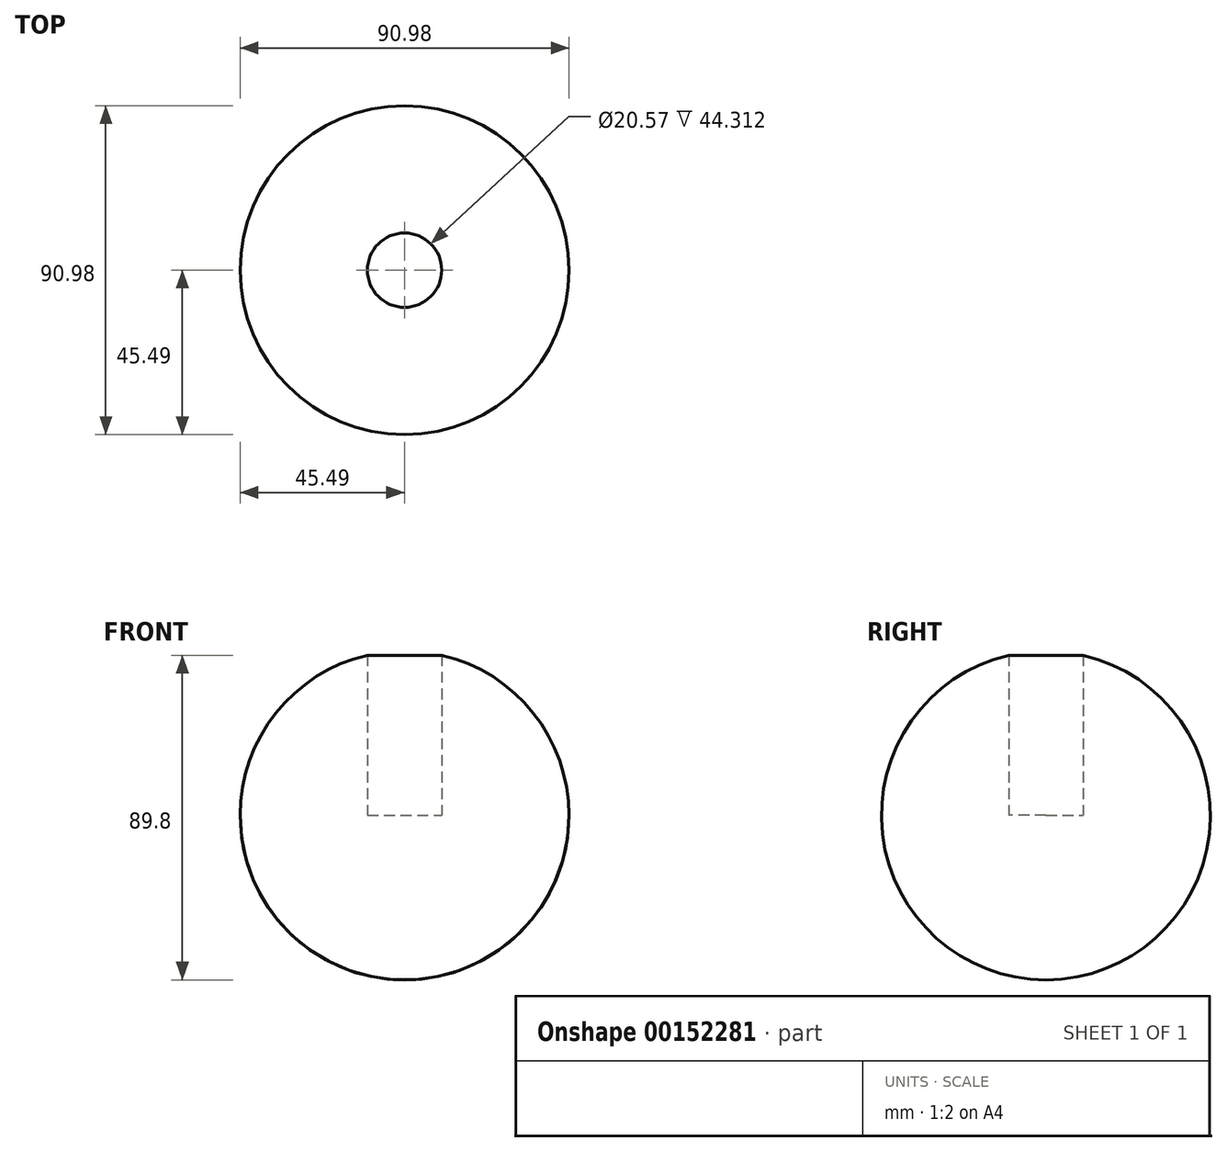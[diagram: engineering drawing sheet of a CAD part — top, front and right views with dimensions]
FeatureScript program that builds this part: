
annotation { "Feature Type Name" : "Feature", "Feature Type Description" : "" }
export const myFeature = defineFeature(function(context is Context, id is Id, definition is map)
    precondition{}
    {
        {
            var Q0;
            Q0=qCreatedBy(makeId("Front.planeOp"),FACE);
            var sketch = newSketch(context, id + "F0", { "sketchPlane" : qUnion([Q0])});
            skArc(sketch, "E0", {"start": v(-45.5, 0) * mm, "mid": v(0, -45.5) * mm, "end": v(45.5, 0) * mm});
            skLineSegment(sketch, "E1.bottom", {"start": v(57.29, -51.39) * mm, "end": v(-57.29, -51.39) * mm});
            skLineSegment(sketch, "E1.left", {"start": v(57.29, -51.39) * mm, "end": v(57.29, 0) * mm});
            skLineSegment(sketch, "E1.right", {"start": v(-57.29, -51.39) * mm, "end": v(-57.29, 0) * mm});
            skPoint(sketch, "E1.top.start.orphan", {"position": v(57.29, 51.39) * mm});
            skPoint(sketch, "E2.orphan", {"position": v(-57.29, 51.39) * mm});
            skLineSegment(sketch, "E3.trimOffspring", {"start": v(45.5, 0) * mm, "end": v(57.29, 0) * mm});
            skLineSegment(sketch, "E4", {"start": v(-57.29, 0) * mm, "end": v(-45.5, 0) * mm});
            skLineSegment(sketch, "E5", {"start": v(-45.5, 0) * mm, "end": v(45.5, 0) * mm});
            skSolve(sketch);
        }
        {
            var Q0;
            Q0=makeQuery(id+"F0.imprint","IMPRINT",FACE,{"disambiguationData":[TD([[makeQuery(id+"F0.imprint","IMPRINT",EDGE,{"derivedFrom":sQuery(id+"F0.wireOp",EDGE,"E0")}),1.0]])]});
            var Q1;
            Q1=sQuery(id+"F0.wireOp",EDGE,"E5");
            revolve(context, id + "F1", {"entities" : qUnion([Q0]), "axis" : qUnion([Q1]), "revolveType" : RevolveType.FULL});
        }
        {
            var Q0;
            Q0=qCreatedBy(makeId("Top.planeOp"),FACE);
            var sketch = newSketch(context, id + "F2", { "sketchPlane" : qUnion([Q0])});
            skCircle(sketch, "E6", {"center": v(0, 0) * mm, "radius": 10.29 * mm});
            skSolve(sketch);
        }
        {
            var Q0;
            Q0 = qSketchRegion(id + "F2", true);
            extrude(context, id + "F3", {"entities" : qUnion([Q0]), "operationType" : NewBodyOperationType.REMOVE, "endBound" : BoundingType.THROUGH_ALL, "depth" : 25.4 * mm});
        }
    });
